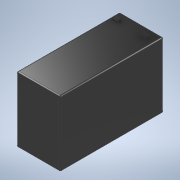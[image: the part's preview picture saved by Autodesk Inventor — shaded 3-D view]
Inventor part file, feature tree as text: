
AUTODESK INVENTOR PART (.ipt)
format: ipt  version: 2021 (Build 250183000, 183)  size: 161,792 bytes
history: native  units: mm
features: extrude x3, sketch x3, fillet x1
ambient origin geometry x8: Origin, YZ Plane, XZ Plane, XY Plane, X Axis, Y Axis, Z Axis, Center Point
bodies: Solid1 (feature_tree)
feature tree (7):
  extrude  "Extrusion1"  Depth=63.0mm
  extrude  "Extrusion2"  Depth=12.0mm
  extrude  "Extrusion3"  Depth=7.0mm
  fillet  "Fillet1"  Radius=2.0mm
  sketch  "Sketch1"  dims[d0=148.0mm d1=63.0mm]
  sketch  "Sketch2"  dims[d2=94.0mm d3=0.0mm d4=12.0mm]
  sketch  "Sketch3"  dims[d5=8.0mm d6=7.0mm d7=2.0mm d8=12.0mm d9=8.0mm d10=2.0mm d11=7.0mm d12=5.0mm d13=0.0mm d14=2.0mm d15=2.0mm d16=5.0mm d17=0.0mm d18=2.0mm]
